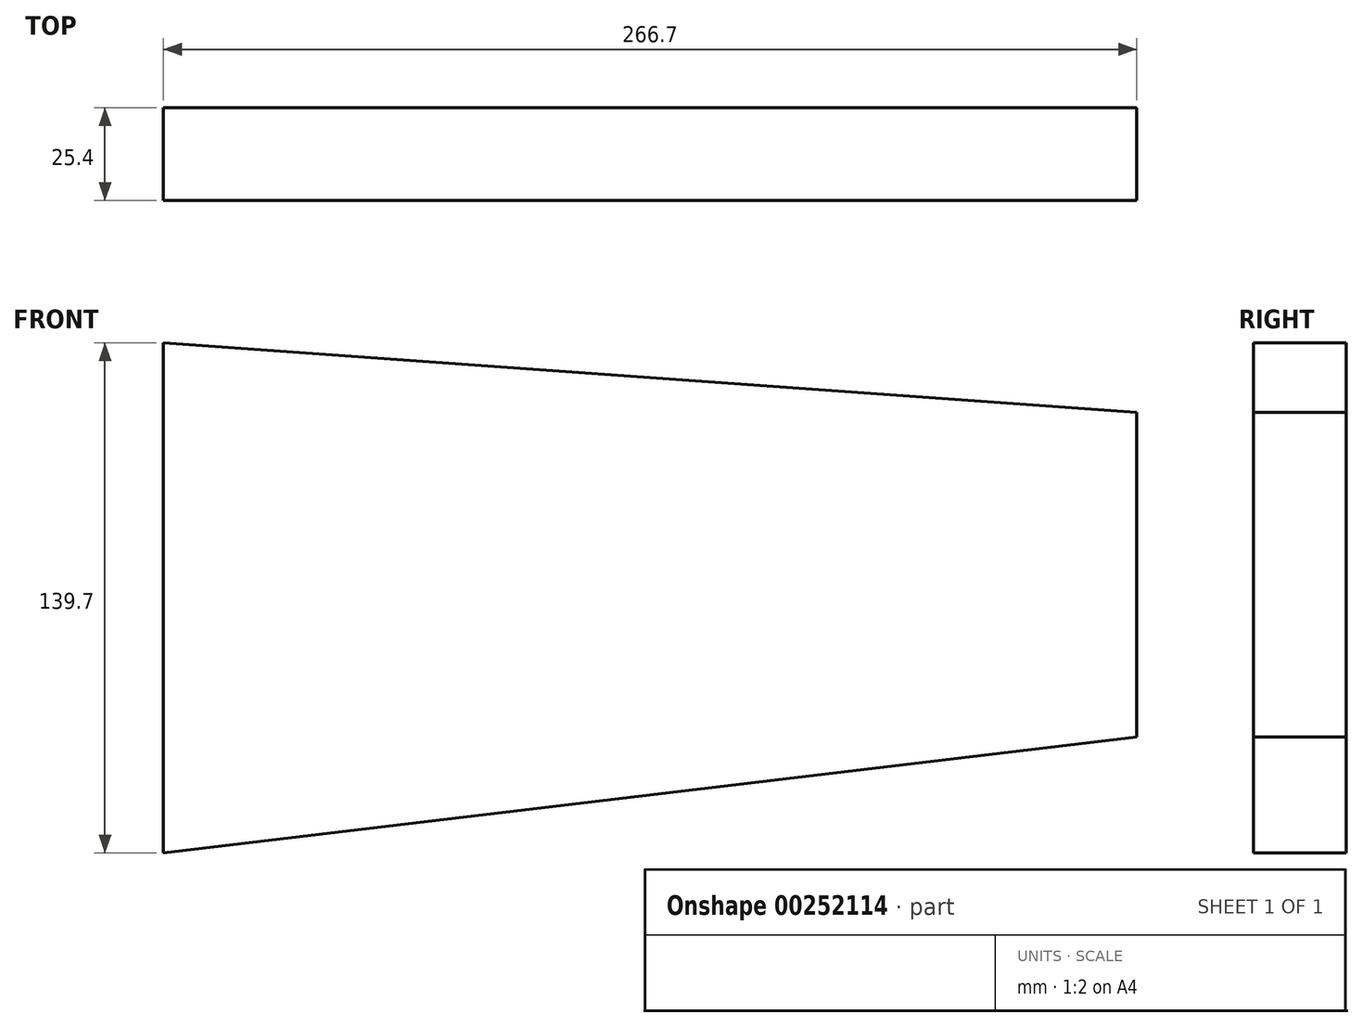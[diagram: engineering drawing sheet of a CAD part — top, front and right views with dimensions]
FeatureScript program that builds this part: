
annotation { "Feature Type Name" : "Feature", "Feature Type Description" : "" }
export const myFeature = defineFeature(function(context is Context, id is Id, definition is map)
    precondition{}
    {
        {
            var Q0;
            Q0=qCreatedBy(makeId("Front.planeOp"),FACE);
            var sketch = newSketch(context, id + "F0", { "sketchPlane" : qUnion([Q0])});
            skLineSegment(sketch, "E0.left", {"start": v(-133.35, 69.85) * mm, "end": v(-133.35, -69.85) * mm});
            skPoint(sketch, "E0.middle", {"position": v(0, 0) * mm});
            skLineSegment(sketch, "E1", {"start": v(133.35, -38.1) * mm, "end": v(-133.35, -69.85) * mm});
            skLineSegment(sketch, "E2", {"start": v(133.35, 50.8) * mm, "end": v(-133.35, 69.85) * mm});
            skFitSpline(sketch, "E3", {"points": [v(133.35, 50.8) * mm, v(133.35, -38.1) * mm], "startDerivative": vector(0, -88.9) * mm, "endDerivative": vector(0, -88.9) * mm});
            skSolve(sketch);
        }
        {
            var Q0;
            Q0=makeQuery(id+"F0.imprint","IMPRINT",FACE,{"disambiguationData":[TD([[makeQuery(id+"F0.imprint","IMPRINT",EDGE,{"derivedFrom":sQuery(id+"F0.wireOp",EDGE,"E0.left")}),1.0]])]});
            extrude(context, id + "F1", {"entities" : qUnion([Q0]), "depth" : 25.4 * mm});
        }
    });
